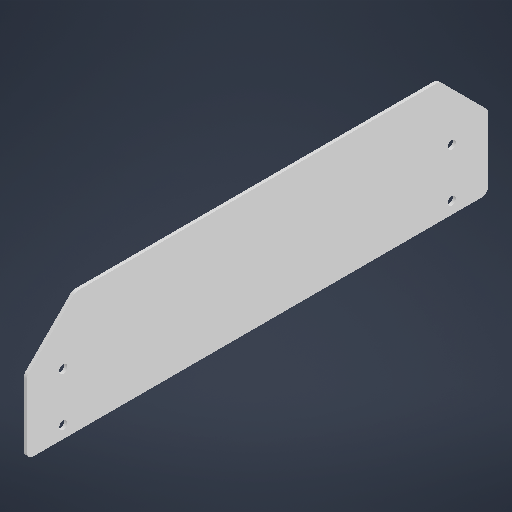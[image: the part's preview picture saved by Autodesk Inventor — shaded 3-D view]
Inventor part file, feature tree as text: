
AUTODESK INVENTOR PART (.ipt)
format: ipt  version: 2025.2 (Build 292293000, 293)  size: 191,488 bytes
history: native  units: in
note: dims shown in document units (in); Inventor stores cm internally (conversion verified against a paired STEP export)
features: extrude x1, sketch x1
ambient origin geometry x8: Origin, YZ Plane, XZ Plane, XY Plane, X Axis, Y Axis, Z Axis, Center Point
bodies: Solid1 (feature_tree)
feature tree (2):
  extrude  "Extrusion1"  Depth=0.0625in TaperAngle=0.0deg
  sketch  "Sketch1"  dims[d0=9.5in d1=1.5in d2=1.5in d3=0.125in d4=0.125in d5=0.125in d6=0.125in d7=0.125in d8=0.125in d9=0.0625in d10=0.0in d15=0.172in d16=0.172in d17=0.172in d18=0.172in]
